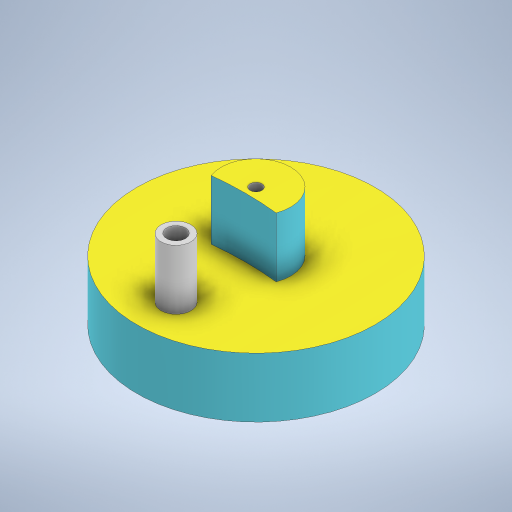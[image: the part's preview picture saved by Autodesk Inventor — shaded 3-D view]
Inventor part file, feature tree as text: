
AUTODESK INVENTOR PART (.ipt)
format: ipt  version: 2023 (Build 270158000, 158)  size: 326,144 bytes
history: native  units: mm
features: extrude x5, sketch x3
ambient origin geometry x8: Origin, YZ Plane, XZ Plane, XY Plane, X Axis, Y Axis, Z Axis, Center Point
bodies: Solid1 (feature_tree)
feature tree (8):
  sketch  "Sketch1"  dims[d1=120.0mm d2=200.0mm d3=15.0deg d4=10.0mm d5=10.0mm d6=79.8mm d7=360.0deg d8=10.0mm d9=4.0mm d10=20.0mm d11=0.0mm]
  extrude  "Extrusion1"  Depth=20.0mm TaperAngle=0.0deg
  extrude  "Extrusion2"  Depth=10.0mm
  extrude  "Extrusion3"  Depth=20.0mm TaperAngle=0.0deg
  extrude  "Extrusion5"  Depth=20.0mm
  extrude  "Extrusion6"  Depth=20.0mm TaperAngle=0.0deg
  sketch  "Sketch2"  dims[d12=20.0mm d13=0.0mm d14=10.0mm]
  sketch  "Sketch4"  dims[d15=20.0mm d16=0.0mm d20=20.0mm d21=0.0mm d22=6.3mm d23=20.0mm d24=0.0mm]
